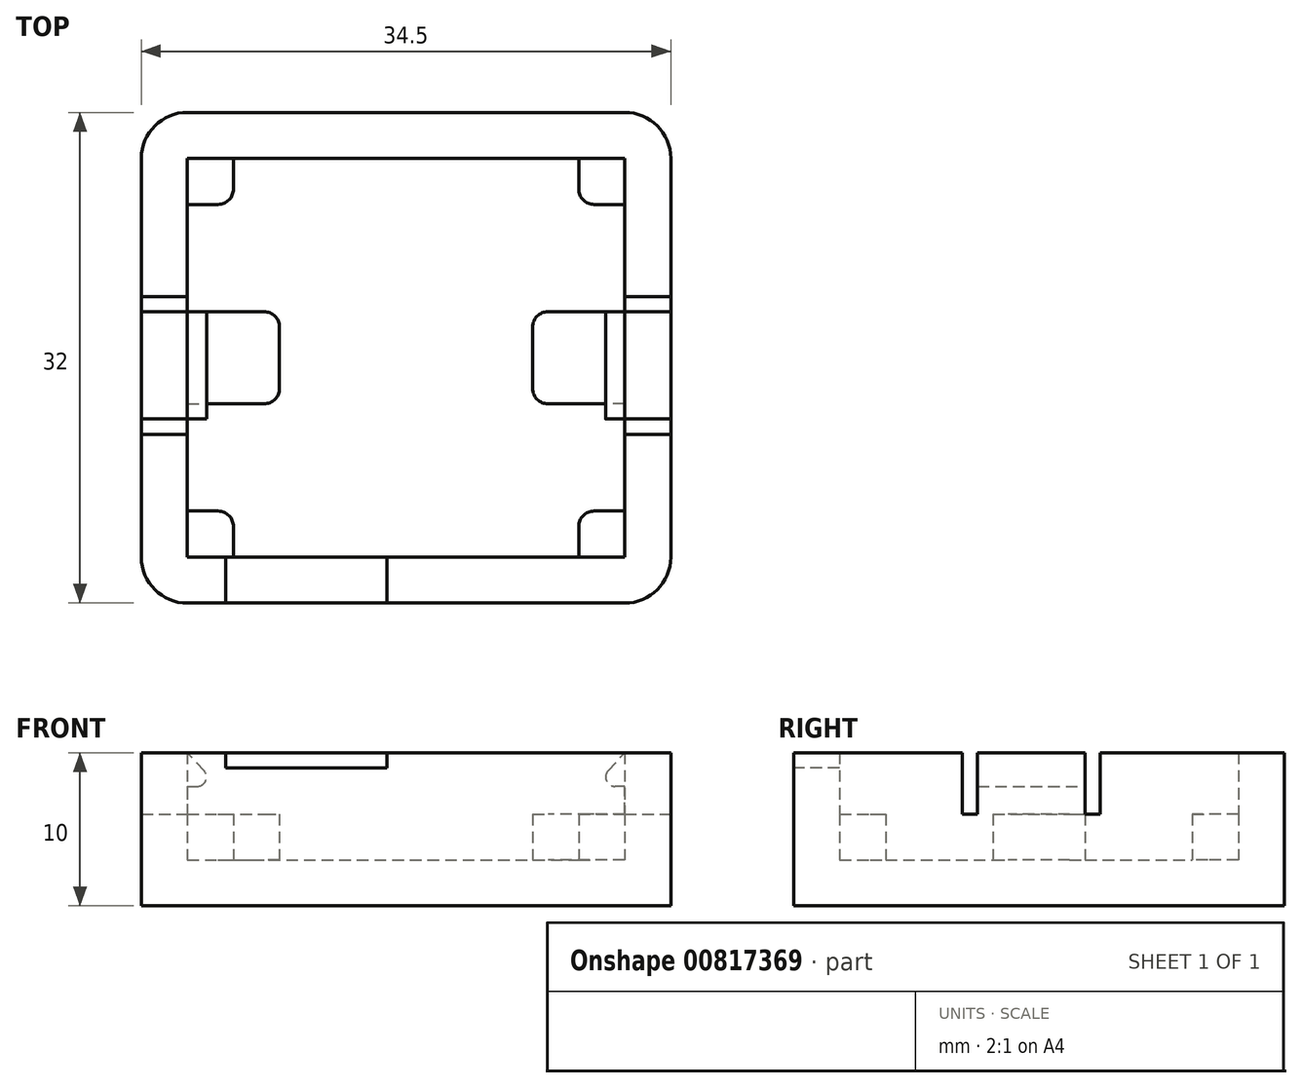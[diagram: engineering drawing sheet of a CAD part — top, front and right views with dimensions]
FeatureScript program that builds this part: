
annotation { "Feature Type Name" : "Feature", "Feature Type Description" : "" }
export const myFeature = defineFeature(function(context is Context, id is Id, definition is map)
    precondition{}
    {
        {
            assignVariable(context, id + "F0", {"name" : "WallThickness", "anyValue" : 3});
        }
        {
            var Q0;
            Q0=qCreatedBy(makeId("Top.planeOp"),FACE);
            var sketch = newSketch(context, id + "F1", { "sketchPlane" : qUnion([Q0])});
            skLineSegment(sketch, "E0.bottom", {"start": v(17.25, 16) * mm, "end": v(-17.25, 16) * mm});
            skLineSegment(sketch, "E0.top", {"start": v(17.25, -16) * mm, "end": v(-17.25, -16) * mm});
            skLineSegment(sketch, "E0.left", {"start": v(17.25, 16) * mm, "end": v(17.25, -16) * mm});
            skLineSegment(sketch, "E0.right", {"start": v(-17.25, 16) * mm, "end": v(-17.25, -16) * mm});
            skPoint(sketch, "E0.middle", {"position": v(0, 0) * mm});
            skSolve(sketch);
        }
        {
            var Q0;
            Q0=makeQuery(id+"F1.imprint","IMPRINT",FACE,{"disambiguationData":[TD([[makeQuery(id+"F1.imprint","IMPRINT",EDGE,{"derivedFrom":sQuery(id+"F1.wireOp",EDGE,"E0.bottom")}),1.0]])]});
            extrude(context, id + "F2", {"entities" : qUnion([Q0]), "depth" : (getVariable(context, 'WallThickness')) * mm, "offsetDistance" : 25 * mm});
        }
        {
            var Q0;
            Q0=makeQuery(id+"F2.opExtrude","SWEPT_EDGE",EDGE,{"disambiguationData":[OSD([sQuery(id+"F1.wireOp",EDGE,"E0.top"),sQuery(id+"F1.wireOp",EDGE,"E0.left")])]});
            var Q1;
            Q1=makeQuery(id+"F2.opExtrude","SWEPT_EDGE",EDGE,{"disambiguationData":[OSD([sQuery(id+"F1.wireOp",EDGE,"E0.top"),sQuery(id+"F1.wireOp",EDGE,"E0.right")])]});
            var Q2;
            Q2=makeQuery(id+"F2.opExtrude","SWEPT_EDGE",EDGE,{"disambiguationData":[OSD([sQuery(id+"F1.wireOp",EDGE,"E0.bottom"),sQuery(id+"F1.wireOp",EDGE,"E0.left")])]});
            var Q3;
            Q3=makeQuery(id+"F2.opExtrude","SWEPT_EDGE",EDGE,{"disambiguationData":[OSD([sQuery(id+"F1.wireOp",EDGE,"E0.bottom"),sQuery(id+"F1.wireOp",EDGE,"E0.right")])]});
            fillet(context, id + "F3", {"entities" : qUnion([Q0, Q1, Q2, Q3]), "radius" : (getVariable(context, 'WallThickness')) * mm, "tangentPropagation" : true, "allowEdgeOverflow" : false});
        }
        {
            var Q0;
            Q0=makeQuery(id+"F2.opExtrude","CAP_FACE",FACE,{"disambiguationData":[OSD([sQuery(id+"F1.wireOp",EDGE,"E0.bottom"),sQuery(id+"F1.wireOp",EDGE,"E0.top"),sQuery(id+"F1.wireOp",EDGE,"E0.left"),sQuery(id+"F1.wireOp",EDGE,"E0.right")])],"isStart":false});
            var sketch = newSketch(context, id + "F4", { "sketchPlane" : qUnion([Q0])});
            skLineSegment(sketch, "E1.0", {"start": v(-14.25, -13) * mm, "end": v(14.25, -13) * mm});
            skLineSegment(sketch, "E1.1", {"start": v(-14.25, 13) * mm, "end": v(-14.25, -13) * mm});
            skLineSegment(sketch, "E1.2", {"start": v(14.25, 13) * mm, "end": v(-14.25, 13) * mm});
            skLineSegment(sketch, "E1.3", {"start": v(14.25, -13) * mm, "end": v(14.25, 13) * mm});
            skSolve(sketch);
        }
        {
            var Q0;
            Q0=makeQuery(id+"F4.imprint","IMPRINT",FACE,{"disambiguationData":[TD([[makeQuery(id+"F4.imprint","IMPRINT",EDGE,{"derivedFrom":sQuery(id+"F4.wireOp",EDGE,"E1.0")}),-1.0]])]});
            extrude(context, id + "F5", {"entities" : qUnion([Q0]), "operationType" : NewBodyOperationType.ADD, "depth" : 7 * mm, "offsetDistance" : 25 * mm});
        }
        {
            var Q0;
            Q0=makeQuery(id+"F2.opExtrude","CAP_FACE",FACE,{"disambiguationData":[OSD([sQuery(id+"F1.wireOp",EDGE,"E0.bottom"),sQuery(id+"F1.wireOp",EDGE,"E0.top"),sQuery(id+"F1.wireOp",EDGE,"E0.left"),sQuery(id+"F1.wireOp",EDGE,"E0.right")])],"isStart":false});
            var sketch = newSketch(context, id + "F6", { "sketchPlane" : qUnion([Q0])});
            skLineSegment(sketch, "E2.bottom", {"start": v(-14.25, 3) * mm, "end": v(-8.25, 3) * mm});
            skLineSegment(sketch, "E2.top", {"start": v(-14.25, -3) * mm, "end": v(-8.25, -3) * mm});
            skLineSegment(sketch, "E2.left", {"start": v(-14.25, 3) * mm, "end": v(-14.25, -3) * mm});
            skLineSegment(sketch, "E2.right", {"start": v(-8.25, 3) * mm, "end": v(-8.25, -3) * mm});
            skPoint(sketch, "E3", {"position": v(-14.25, 0) * mm});
            skLineSegment(sketch, "E4.MirrorCS", {"start": v(14.25, -3) * mm, "end": v(8.25, -3) * mm});
            skLineSegment(sketch, "E5.MirrorCS", {"start": v(14.25, 3) * mm, "end": v(14.25, -3) * mm});
            skLineSegment(sketch, "E6.MirrorCS", {"start": v(8.25, 3) * mm, "end": v(8.25, -3) * mm});
            skPoint(sketch, "E7.MirrorP", {"position": v(14.25, 0) * mm});
            skLineSegment(sketch, "E8.MirrorCS", {"start": v(14.25, 3) * mm, "end": v(8.25, 3) * mm});
            skLineSegment(sketch, "E9.bottom", {"start": v(-14.25, 13) * mm, "end": v(-11.25, 13) * mm});
            skLineSegment(sketch, "E9.top", {"start": v(-14.25, 10) * mm, "end": v(-11.25, 10) * mm});
            skLineSegment(sketch, "E9.left", {"start": v(-14.25, 13) * mm, "end": v(-14.25, 10) * mm});
            skLineSegment(sketch, "E9.right", {"start": v(-11.25, 13) * mm, "end": v(-11.25, 10) * mm});
            skLineSegment(sketch, "E10.bottom", {"start": v(-14.25, -13) * mm, "end": v(-11.25, -13) * mm});
            skLineSegment(sketch, "E10.top", {"start": v(-14.25, -10) * mm, "end": v(-11.25, -10) * mm});
            skLineSegment(sketch, "E10.left", {"start": v(-14.25, -13) * mm, "end": v(-14.25, -10) * mm});
            skLineSegment(sketch, "E10.right", {"start": v(-11.25, -13) * mm, "end": v(-11.25, -10) * mm});
            skLineSegment(sketch, "E11.bottom", {"start": v(14.25, -13) * mm, "end": v(11.25, -13) * mm});
            skLineSegment(sketch, "E11.top", {"start": v(14.25, -10) * mm, "end": v(11.25, -10) * mm});
            skLineSegment(sketch, "E11.left", {"start": v(14.25, -13) * mm, "end": v(14.25, -10) * mm});
            skLineSegment(sketch, "E11.right", {"start": v(11.25, -13) * mm, "end": v(11.25, -10) * mm});
            skLineSegment(sketch, "E12.bottom", {"start": v(14.25, 13) * mm, "end": v(11.25, 13) * mm});
            skLineSegment(sketch, "E12.top", {"start": v(14.25, 10) * mm, "end": v(11.25, 10) * mm});
            skLineSegment(sketch, "E12.left", {"start": v(14.25, 13) * mm, "end": v(14.25, 10) * mm});
            skLineSegment(sketch, "E12.right", {"start": v(11.25, 13) * mm, "end": v(11.25, 10) * mm});
            skSolve(sketch);
        }
        {
            var Q0;
            Q0=makeQuery(id+"F6.imprint","IMPRINT",FACE,{"disambiguationData":[TD([[makeQuery(id+"F6.imprint","IMPRINT",EDGE,{"derivedFrom":sQuery(id+"F6.wireOp",EDGE,"E2.bottom")}),-1.0]])]});
            var Q1;
            Q1=makeQuery(id+"F6.imprint","IMPRINT",FACE,{"disambiguationData":[TD([[makeQuery(id+"F6.imprint","IMPRINT",EDGE,{"derivedFrom":sQuery(id+"F6.wireOp",EDGE,"E4.MirrorCS")}),-1.0]])]});
            var Q2;
            Q2=makeQuery(id+"F6.imprint","IMPRINT",FACE,{"disambiguationData":[TD([[makeQuery(id+"F6.imprint","IMPRINT",EDGE,{"derivedFrom":sQuery(id+"F6.wireOp",EDGE,"E9.bottom")}),1.0]])]});
            var Q3;
            Q3=makeQuery(id+"F6.imprint","IMPRINT",FACE,{"disambiguationData":[TD([[makeQuery(id+"F6.imprint","IMPRINT",EDGE,{"derivedFrom":sQuery(id+"F6.wireOp",EDGE,"E12.bottom")}),1.0]])]});
            var Q4;
            Q4=makeQuery(id+"F6.imprint","IMPRINT",FACE,{"disambiguationData":[TD([[makeQuery(id+"F6.imprint","IMPRINT",EDGE,{"derivedFrom":sQuery(id+"F6.wireOp",EDGE,"E10.bottom")}),1.0]])]});
            var Q5;
            Q5=makeQuery(id+"F6.imprint","IMPRINT",FACE,{"disambiguationData":[TD([[makeQuery(id+"F6.imprint","IMPRINT",EDGE,{"derivedFrom":sQuery(id+"F6.wireOp",EDGE,"E11.bottom")}),1.0]])]});
            extrude(context, id + "F7", {"entities" : qUnion([Q0, Q1, Q2, Q3, Q4, Q5]), "operationType" : NewBodyOperationType.ADD, "depth" : 3 * mm, "offsetDistance" : 25 * mm});
        }
        {
            var Q0;
            {var subQ0=sQuery(id+"F1.wireOp",EDGE,"E0.top");Q0=makeQuery(id+"F5.boolean.opBoolean","MERGE",FACE,{"derivedFrom":[makeQuery(id+"F2.opExtrude","SWEPT_FACE",FACE,{"disambiguationData":[OSD([subQ0])]}),makeQuery(id+"F5.opExtrude","SWEPT_FACE",FACE,{"disambiguationData":[OSD([subQ0])]})]});}
            var sketch = newSketch(context, id + "F8", { "sketchPlane" : qUnion([Q0])});
            skLineSegment(sketch, "E13.bottom", {"start": v(-11.75, 10) * mm, "end": v(-1.25, 10) * mm});
            skLineSegment(sketch, "E13.top", {"start": v(-11.75, 9) * mm, "end": v(-1.25, 9) * mm});
            skLineSegment(sketch, "E13.left", {"start": v(-11.75, 10) * mm, "end": v(-11.75, 9) * mm});
            skLineSegment(sketch, "E13.right", {"start": v(-1.25, 10) * mm, "end": v(-1.25, 9) * mm});
            skSolve(sketch);
        }
        {
            var Q0;
            Q0=makeQuery(id+"F8.imprint","IMPRINT",FACE,{"disambiguationData":[TD([[makeQuery(id+"F8.imprint","IMPRINT",EDGE,{"derivedFrom":sQuery(id+"F8.wireOp",EDGE,"E13.bottom")}),1.0]])]});
            extrude(context, id + "F9", {"entities" : qUnion([Q0]), "operationType" : NewBodyOperationType.REMOVE, "endBound" : BoundingType.UP_TO_NEXT, "oppositeDirection" : true, "depth" : 25 * mm, "offsetDistance" : 25 * mm});
        }
        {
            var Q0;
            {var subQ0=sQuery(id+"F1.wireOp",EDGE,"E0.left");Q0=makeQuery(id+"F5.boolean.opBoolean","MERGE",FACE,{"derivedFrom":[makeQuery(id+"F2.opExtrude","SWEPT_FACE",FACE,{"disambiguationData":[OSD([subQ0])]}),makeQuery(id+"F5.opExtrude","SWEPT_FACE",FACE,{"disambiguationData":[OSD([subQ0])]})]});}
            var sketch = newSketch(context, id + "F10", { "sketchPlane" : qUnion([Q0])});
            skLineSegment(sketch, "E14.bottom", {"start": v(-4, 10) * mm, "end": v(-5, 10) * mm});
            skLineSegment(sketch, "E14.top", {"start": v(-4, 6) * mm, "end": v(-5, 6) * mm});
            skLineSegment(sketch, "E14.left", {"start": v(-4, 10) * mm, "end": v(-4, 6) * mm});
            skLineSegment(sketch, "E14.right", {"start": v(-5, 10) * mm, "end": v(-5, 6) * mm});
            skLineSegment(sketch, "E15.bottom", {"start": v(3, 10) * mm, "end": v(4, 10) * mm});
            skLineSegment(sketch, "E15.top", {"start": v(3, 6) * mm, "end": v(4, 6) * mm});
            skLineSegment(sketch, "E15.left", {"start": v(3, 10) * mm, "end": v(3, 6) * mm});
            skLineSegment(sketch, "E15.right", {"start": v(4, 10) * mm, "end": v(4, 6) * mm});
            skSolve(sketch);
        }
        {
            var Q0;
            Q0 = qSketchRegion(id + "F10", true);
            var Q1;
            {var subQ0=sQuery(id+"F1.wireOp",EDGE,"E0.right");Q1=makeQuery(id+"F5.boolean.opBoolean","MERGE",FACE,{"derivedFrom":[makeQuery(id+"F2.opExtrude","SWEPT_FACE",FACE,{"disambiguationData":[OSD([subQ0])]}),makeQuery(id+"F5.opExtrude","SWEPT_FACE",FACE,{"disambiguationData":[OSD([subQ0])]})]});}
            extrude(context, id + "F11", {"entities" : qUnion([Q0]), "operationType" : NewBodyOperationType.REMOVE, "endBound" : BoundingType.UP_TO_SURFACE, "oppositeDirection" : true, "depth" : 25 * mm, "endBoundEntityFace" : qUnion([Q1]), "offsetDistance" : 25 * mm});
        }
        {
            var Q0;
            {var subQ0=sQuery(id+"F1.wireOp",EDGE,"E0.left");Q0=makeQuery(id+"F11.boolean.opBoolean","COPY",FACE,{"disambiguationData":[TD([makeQuery(id+"F2.opExtrude","SWEPT_FACE",FACE,{"disambiguationData":[OSD([subQ0])]})])],"derivedFrom":makeQuery(id+"F11.opExtrude","SWEPT_FACE",FACE,{"disambiguationData":[OSD([sQuery(id+"F10.wireOp",EDGE,"E15.left")])]})});}
            var sketch = newSketch(context, id + "F12", { "sketchPlane" : qUnion([Q0])});
            skLineSegment(sketch, "E16", {"start": v(-14.25, 7.8) * mm, "end": v(-12.25, 7.8) * mm});
            skLineSegment(sketch, "E17", {"start": v(-12.25, 7.8) * mm, "end": v(-14.25, 10) * mm});
            skLineSegment(sketch, "E18", {"start": v(-14.25, 7.8) * mm, "end": v(-14.25, 10) * mm});
            skLineSegment(sketch, "E19.MirrorCS", {"start": v(12.25, 7.8) * mm, "end": v(14.25, 10) * mm});
            skLineSegment(sketch, "E20.MirrorCS", {"start": v(14.25, 7.8) * mm, "end": v(14.25, 10) * mm});
            skLineSegment(sketch, "E21.MirrorCS", {"start": v(14.25, 7.8) * mm, "end": v(12.25, 7.8) * mm});
            skSolve(sketch);
        }
        {
            var Q0;
            Q0=makeQuery(id+"F12.imprint","IMPRINT",FACE,{"disambiguationData":[TD([[makeQuery(id+"F12.imprint","IMPRINT",EDGE,{"derivedFrom":sQuery(id+"F12.wireOp",EDGE,"E16")}),1.0]])]});
            var Q1;
            Q1=makeQuery(id+"F12.imprint","IMPRINT",FACE,{"disambiguationData":[TD([[makeQuery(id+"F12.imprint","IMPRINT",EDGE,{"derivedFrom":sQuery(id+"F12.wireOp",EDGE,"E19.MirrorCS")}),-1.0]])]});
            var Q2;
            {var subQ0=sQuery(id+"F1.wireOp",EDGE,"E0.left");Q2=makeQuery(id+"F11.boolean.opBoolean","COPY",FACE,{"disambiguationData":[TD([makeQuery(id+"F2.opExtrude","SWEPT_FACE",FACE,{"disambiguationData":[OSD([subQ0])]})])],"derivedFrom":makeQuery(id+"F11.opExtrude","SWEPT_FACE",FACE,{"disambiguationData":[OSD([sQuery(id+"F10.wireOp",EDGE,"E14.left")])]})});}
            extrude(context, id + "F13", {"entities" : qUnion([Q0, Q1]), "operationType" : NewBodyOperationType.ADD, "endBound" : BoundingType.UP_TO_SURFACE, "oppositeDirection" : true, "depth" : 25 * mm, "endBoundEntityFace" : qUnion([Q2]), "offsetDistance" : 25 * mm});
        }
        {
            var Q0;
            Q0=makeQuery(id+"F7.opExtrude","SWEPT_EDGE",EDGE,{"disambiguationData":[OSD([sQuery(id+"F6.wireOp",EDGE,"E6.MirrorCS"),sQuery(id+"F6.wireOp",EDGE,"E8.MirrorCS")])]});
            var Q1;
            Q1=makeQuery(id+"F7.opExtrude","SWEPT_EDGE",EDGE,{"disambiguationData":[OSD([sQuery(id+"F6.wireOp",EDGE,"E4.MirrorCS"),sQuery(id+"F6.wireOp",EDGE,"E6.MirrorCS")])]});
            var Q2;
            Q2=makeQuery(id+"F7.opExtrude","SWEPT_EDGE",EDGE,{"disambiguationData":[OSD([sQuery(id+"F6.wireOp",EDGE,"E11.top"),sQuery(id+"F6.wireOp",EDGE,"E11.right")])]});
            var Q3;
            Q3=makeQuery(id+"F7.opExtrude","SWEPT_EDGE",EDGE,{"disambiguationData":[OSD([sQuery(id+"F6.wireOp",EDGE,"E12.top"),sQuery(id+"F6.wireOp",EDGE,"E12.right")])]});
            var Q4;
            Q4=makeQuery(id+"F7.opExtrude","SWEPT_EDGE",EDGE,{"disambiguationData":[OSD([sQuery(id+"F6.wireOp",EDGE,"E10.top"),sQuery(id+"F6.wireOp",EDGE,"E10.right")])]});
            var Q5;
            Q5=makeQuery(id+"F7.opExtrude","SWEPT_EDGE",EDGE,{"disambiguationData":[OSD([sQuery(id+"F6.wireOp",EDGE,"E9.top"),sQuery(id+"F6.wireOp",EDGE,"E9.right")])]});
            var Q6;
            Q6=makeQuery(id+"F7.opExtrude","SWEPT_EDGE",EDGE,{"disambiguationData":[OSD([sQuery(id+"F6.wireOp",EDGE,"E2.bottom"),sQuery(id+"F6.wireOp",EDGE,"E2.right")])]});
            var Q7;
            Q7=makeQuery(id+"F7.opExtrude","SWEPT_EDGE",EDGE,{"disambiguationData":[OSD([sQuery(id+"F6.wireOp",EDGE,"E2.top"),sQuery(id+"F6.wireOp",EDGE,"E2.right")])]});
            fillet(context, id + "F14", {"entities" : qUnion([Q0, Q1, Q2, Q3, Q4, Q5, Q6, Q7]), "radius" : 1 * mm, "tangentPropagation" : true, "allowEdgeOverflow" : false});
        }
        {
            var Q0;
            Q0=makeQuery(id+"F13.opExtrude","SWEPT_EDGE",EDGE,{"disambiguationData":[OSD([sQuery(id+"F12.wireOp",EDGE,"E16"),sQuery(id+"F12.wireOp",EDGE,"E17")])]});
            var Q1;
            Q1=makeQuery(id+"F13.opExtrude","SWEPT_EDGE",EDGE,{"disambiguationData":[OSD([sQuery(id+"F12.wireOp",EDGE,"E19.MirrorCS"),sQuery(id+"F12.wireOp",EDGE,"E21.MirrorCS")])]});
            fillet(context, id + "F15", {"entities" : qUnion([Q0, Q1]), "radius" : 0.6 * mm, "tangentPropagation" : true, "allowEdgeOverflow" : false});
        }
    });
